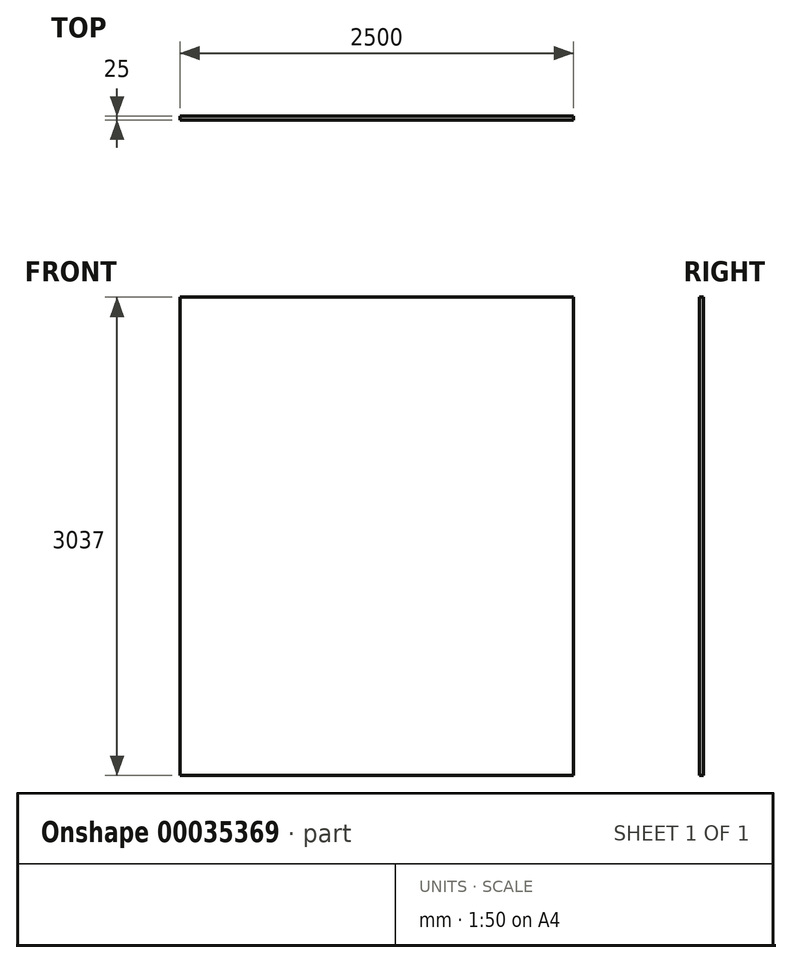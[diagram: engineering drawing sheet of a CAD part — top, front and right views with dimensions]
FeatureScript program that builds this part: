
annotation { "Feature Type Name" : "Feature", "Feature Type Description" : "" }
export const myFeature = defineFeature(function(context is Context, id is Id, definition is map)
    precondition{}
    {
        {
            var Q0;
            Q0=qCreatedBy(makeId("Front.planeOp"),FACE);
            var sketch = newSketch(context, id + "F0", { "sketchPlane" : qUnion([Q0])});
            skLineSegment(sketch, "E0.rect.bottom", {"start": v(1250, -1518.5) * mm, "end": v(-1250, -1518.5) * mm});
            skLineSegment(sketch, "E0.rect.top", {"start": v(1250, 1518.5) * mm, "end": v(-1250, 1518.5) * mm});
            skLineSegment(sketch, "E0.rect.left", {"start": v(1250, -1518.5) * mm, "end": v(1250, 1518.5) * mm});
            skLineSegment(sketch, "E0.rect.right", {"start": v(-1250, -1518.5) * mm, "end": v(-1250, 1518.5) * mm});
            skPoint(sketch, "E0.rect.middle", {"position": v(0, 0) * mm});
            skSolve(sketch);
        }
        {
            var Q0;
            Q0=makeQuery(id+"F0.imprint","IMPRINT",FACE,{"disambiguationData":[TD([[makeQuery(id+"F0.imprint","IMPRINT",EDGE,{"derivedFrom":sQuery(id+"F0.wireOp",EDGE,"E0.rect.bottom")}),-1.0]])]});
            extrude(context, id + "F1", {"entities" : qUnion([Q0]), "depth" : 25 * mm});
        }
    });
